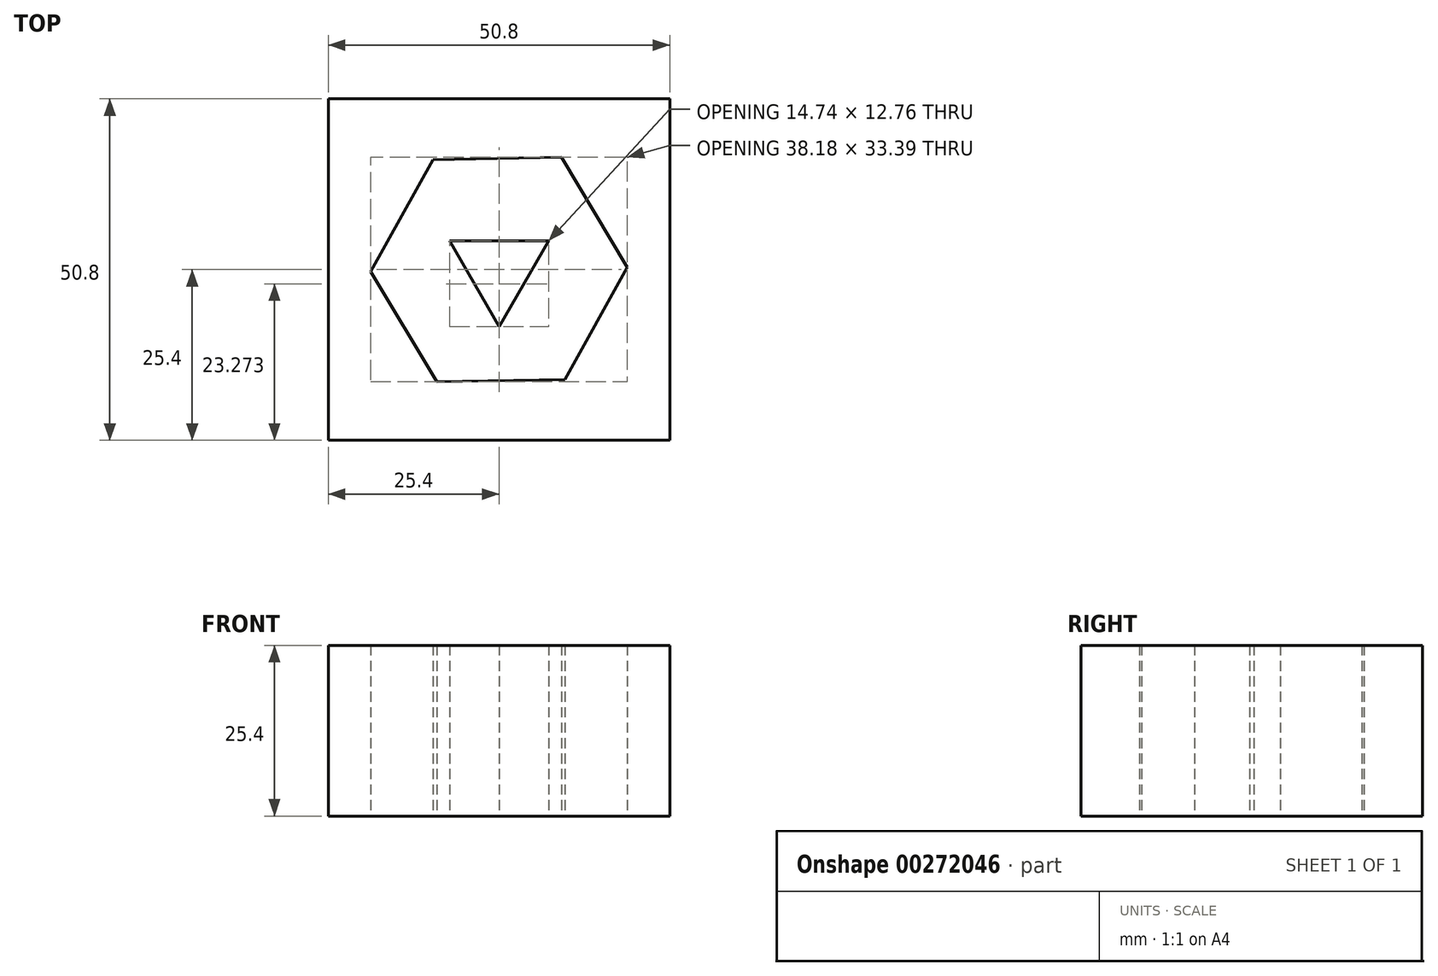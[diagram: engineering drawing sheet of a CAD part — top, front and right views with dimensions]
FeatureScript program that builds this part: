
annotation { "Feature Type Name" : "Feature", "Feature Type Description" : "" }
export const myFeature = defineFeature(function(context is Context, id is Id, definition is map)
    precondition{}
    {
        {
            var Q0;
            Q0=qCreatedBy(makeId("Top.planeOp"),FACE);
            var sketch = newSketch(context, id + "F0", { "sketchPlane" : qUnion([Q0])});
            skLineSegment(sketch, "E0.bottom", {"start": v(25.4, 25.4) * mm, "end": v(-25.4, 25.4) * mm});
            skLineSegment(sketch, "E0.top", {"start": v(25.4, -25.4) * mm, "end": v(-25.4, -25.4) * mm});
            skLineSegment(sketch, "E0.left", {"start": v(25.4, 25.4) * mm, "end": v(25.4, -25.4) * mm});
            skLineSegment(sketch, "E0.right", {"start": v(-25.4, 25.4) * mm, "end": v(-25.4, -25.4) * mm});
            skPoint(sketch, "E0.middle", {"position": v(0, 0) * mm});
            skLineSegment(sketch, "E1.0", {"start": v(9.27, 16.7) * mm, "end": v(19.1, 0.32) * mm});
            skLineSegment(sketch, "E1.1", {"start": v(19.1, 0.32) * mm, "end": v(9.82, -16.37) * mm});
            skLineSegment(sketch, "E1.2", {"start": v(9.82, -16.37) * mm, "end": v(-9.27, -16.7) * mm});
            skLineSegment(sketch, "E1.3", {"start": v(-9.27, -16.7) * mm, "end": v(-19.1, -0.32) * mm});
            skLineSegment(sketch, "E1.4", {"start": v(-19.1, -0.32) * mm, "end": v(-9.82, 16.37) * mm});
            skLineSegment(sketch, "E1.5", {"start": v(-9.82, 16.37) * mm, "end": v(9.27, 16.7) * mm});
            skPoint(sketch, "E1.0.midPoint", {"position": v(14.18, 8.5) * mm});
            skLineSegment(sketch, "E2.0", {"start": v(-7.37, 4.25) * mm, "end": v(7.37, 4.25) * mm});
            skLineSegment(sketch, "E2.1", {"start": v(7.37, 4.25) * mm, "end": v(0, -8.5) * mm});
            skLineSegment(sketch, "E2.2", {"start": v(0, -8.5) * mm, "end": v(-7.37, 4.25) * mm});
            skPoint(sketch, "E2.0.midPoint", {"position": v(0, 4.25) * mm});
            skSolve(sketch);
        }
        {
            var Q0;
            Q0=makeQuery(id+"F0.imprint","IMPRINT",FACE,{"disambiguationData":[TD([[makeQuery(id+"F0.imprint","IMPRINT",EDGE,{"derivedFrom":sQuery(id+"F0.wireOp",EDGE,"E0.bottom")}),1.0]])]});
            extrude(context, id + "F1", {"entities" : qUnion([Q0]), "depth" : 25.4 * mm});
        }
        {
            var Q0;
            Q0=makeQuery(id+"F0.imprint","IMPRINT",FACE,{"disambiguationData":[TD([[makeQuery(id+"F0.imprint","IMPRINT",EDGE,{"derivedFrom":sQuery(id+"F0.wireOp",EDGE,"E1.0")}),-1.0]])]});
            extrude(context, id + "F2", {"entities" : qUnion([Q0]), "depth" : 25.4 * mm});
        }
        {
            var Q0;
            Q0=makeQuery(id+"F0.imprint","IMPRINT",FACE,{"disambiguationData":[TD([[makeQuery(id+"F0.imprint","IMPRINT",EDGE,{"derivedFrom":sQuery(id+"F0.wireOp",EDGE,"E2.0")}),-1.0]])]});
            extrude(context, id + "F3", {"entities" : qUnion([Q0]), "depth" : 25.4 * mm});
        }
    });
